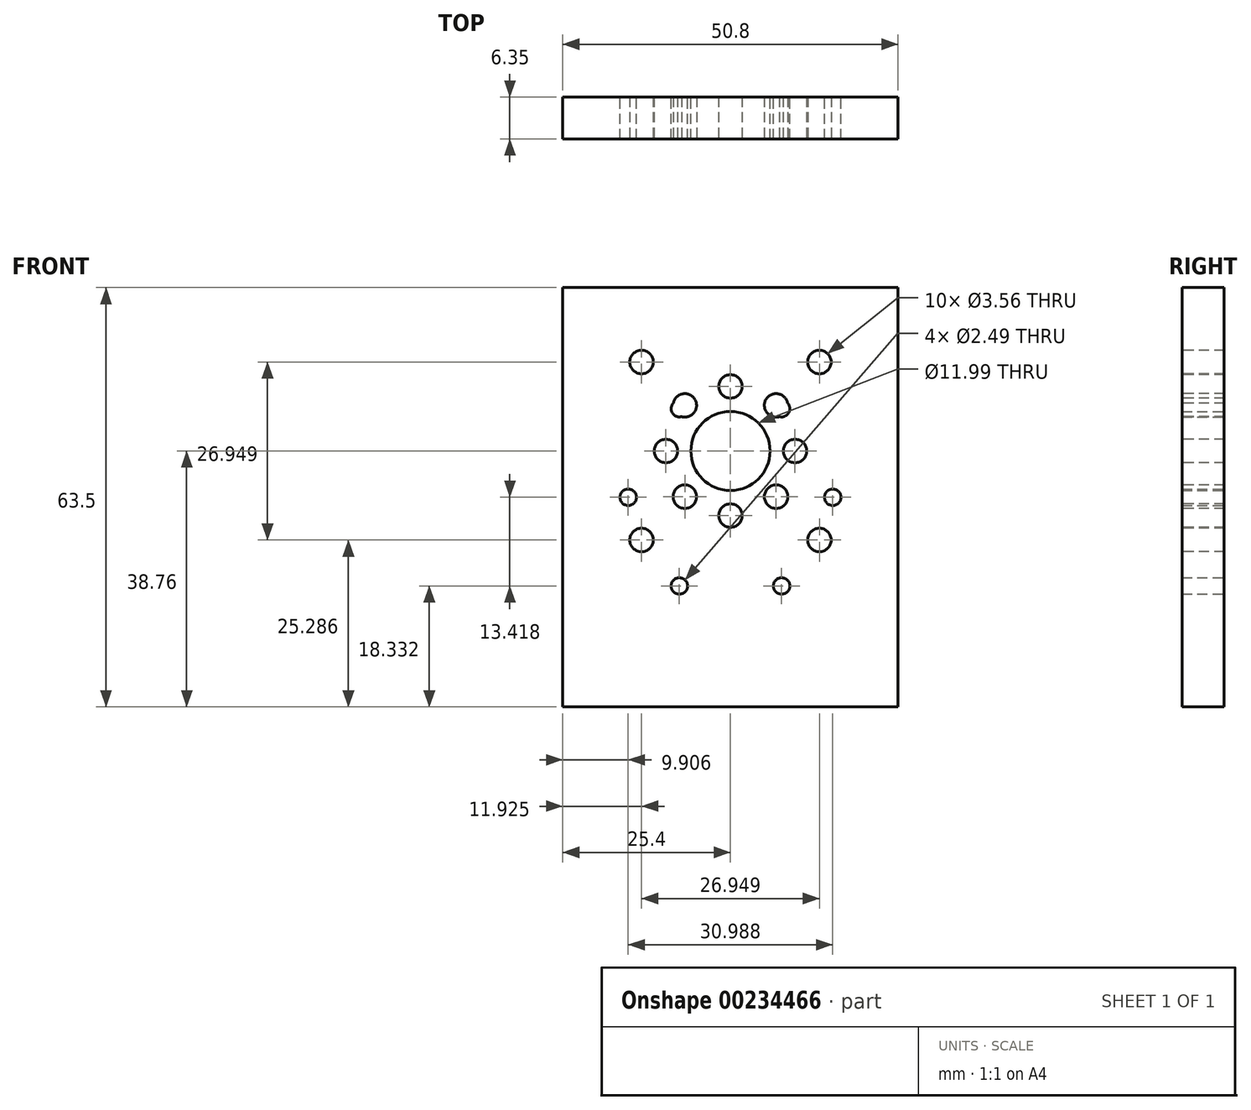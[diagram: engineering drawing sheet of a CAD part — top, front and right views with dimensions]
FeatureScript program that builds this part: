
annotation { "Feature Type Name" : "Feature", "Feature Type Description" : "" }
export const myFeature = defineFeature(function(context is Context, id is Id, definition is map)
    precondition{}
    {
        {
            var Q0;
            Q0=qCreatedBy(makeId("Front.planeOp"),FACE);
            var sketch = newSketch(context, id + "F0", { "sketchPlane" : qUnion([Q0])});
            skLineSegment(sketch, "E0.bottom", {"start": v(25.4, -31.75) * mm, "end": v(-25.4, -31.75) * mm});
            skLineSegment(sketch, "E0.top", {"start": v(25.4, 31.75) * mm, "end": v(-25.4, 31.75) * mm});
            skLineSegment(sketch, "E0.left", {"start": v(25.4, -31.75) * mm, "end": v(25.4, 31.75) * mm});
            skLineSegment(sketch, "E0.right", {"start": v(-25.4, -31.75) * mm, "end": v(-25.4, 31.75) * mm});
            skPoint(sketch, "E0.middle", {"position": v(0, 0) * mm});
            skCircle(sketch, "E1", {"center": v(0, 0) * mm, "radius": 15.5 * mm, "construction": true});
            skCircle(sketch, "E2", {"center": v(-15.5, 0) * mm, "radius": 1.24 * mm});
            skCircle(sketch, "E3.1.0", {"center": v(-7.75, -13.42) * mm, "radius": 1.24 * mm});
            skCircle(sketch, "E3.2.0", {"center": v(7.75, -13.42) * mm, "radius": 1.24 * mm});
            skCircle(sketch, "E3.3.0", {"center": v(15.5, 0) * mm, "radius": 1.24 * mm});
            skCircle(sketch, "E3.4.0", {"center": v(7.75, 13.42) * mm, "radius": 1.24 * mm});
            skCircle(sketch, "E3.5.0", {"center": v(-7.75, 13.42) * mm, "radius": 1.24 * mm});
            skSolve(sketch);
        }
        {
            var Q0;
            Q0=makeQuery(id+"F0.imprint","IMPRINT",FACE,{"disambiguationData":[TD([[makeQuery(id+"F0.imprint","IMPRINT",EDGE,{"derivedFrom":sQuery(id+"F0.wireOp",EDGE,"E0.bottom")}),-1.0]])]});
            var sketch = newSketch(context, id + "F1", { "sketchPlane" : qUnion([Q0])});
            skCircle(sketch, "E4", {"center": v(0, 7.01) * mm, "radius": 6 * mm});
            skSolve(sketch);
        }
        {
            var Q0;
            Q0=makeQuery(id+"F1.imprint","IMPRINT",FACE,{"disambiguationData":[TD([[makeQuery(id+"F1.imprint","IMPRINT",EDGE,{"derivedFrom":sQuery(id+"F1.wireOp",EDGE,"E4")}),-1.0]])]});
            extrude(context, id + "F2", {"entities" : qUnion([Q0]), "depth" : 6.35 * mm});
        }
        {
            var Q0;
            Q0=makeQuery(id+"F2.opExtrude","CAP_FACE",FACE,{"disambiguationData":[OSD([sQuery(id+"F0.wireOp",EDGE,"E0.bottom"),sQuery(id+"F0.wireOp",EDGE,"E0.top"),sQuery(id+"F0.wireOp",EDGE,"E0.left"),sQuery(id+"F0.wireOp",EDGE,"E0.right"),sQuery(id+"F0.wireOp",EDGE,"E2"),sQuery(id+"F0.wireOp",EDGE,"E3.1.0"),sQuery(id+"F0.wireOp",EDGE,"E3.2.0"),sQuery(id+"F0.wireOp",EDGE,"E3.3.0"),sQuery(id+"F0.wireOp",EDGE,"E3.4.0"),sQuery(id+"F0.wireOp",EDGE,"E3.5.0"),sQuery(id+"F1.wireOp",EDGE,"E4")])],"isStart":false});
            var sketch = newSketch(context, id + "F3", { "sketchPlane" : qUnion([Q0])});
            skCircle(sketch, "E5", {"center": v(0, 7.01) * mm, "radius": 9.78 * mm, "construction": true});
            skCircle(sketch, "E6", {"center": v(-9.78, 7.01) * mm, "radius": 1.78 * mm});
            skCircle(sketch, "E7.1.0", {"center": v(-6.91, 0.1) * mm, "radius": 1.78 * mm});
            skCircle(sketch, "E7.2.0", {"center": v(0, -2.77) * mm, "radius": 1.78 * mm});
            skCircle(sketch, "E7.3.0", {"center": v(6.91, 0.1) * mm, "radius": 1.78 * mm});
            skCircle(sketch, "E7.4.0", {"center": v(9.78, 7.01) * mm, "radius": 1.78 * mm});
            skCircle(sketch, "E7.5.0", {"center": v(6.91, 13.93) * mm, "radius": 1.78 * mm});
            skCircle(sketch, "E8.1.6.0", {"center": v(0, 16.79) * mm, "radius": 1.78 * mm});
            skCircle(sketch, "E8.1.7.0", {"center": v(-6.91, 13.93) * mm, "radius": 1.78 * mm});
            skLineSegment(sketch, "E9.bottom", {"start": v(13.47, -6.46) * mm, "end": v(-13.47, -6.46) * mm, "construction": true});
            skLineSegment(sketch, "E9.top", {"start": v(13.47, 20.49) * mm, "end": v(-13.47, 20.49) * mm, "construction": true});
            skLineSegment(sketch, "E9.left", {"start": v(13.47, -6.46) * mm, "end": v(13.47, 20.49) * mm, "construction": true});
            skLineSegment(sketch, "E9.right", {"start": v(-13.47, -6.46) * mm, "end": v(-13.47, 20.49) * mm, "construction": true});
            skCircle(sketch, "E10", {"center": v(-13.47, 20.49) * mm, "radius": 1.78 * mm});
            skCircle(sketch, "E11", {"center": v(13.47, 20.49) * mm, "radius": 1.78 * mm});
            skCircle(sketch, "E12", {"center": v(13.47, -6.46) * mm, "radius": 1.78 * mm});
            skCircle(sketch, "E13", {"center": v(-13.47, -6.46) * mm, "radius": 1.78 * mm});
            skSolve(sketch);
        }
        {
            var Q0;
            Q0 = qSketchRegion(id + "F3", true);
            extrude(context, id + "F4", {"entities" : qUnion([Q0]), "operationType" : NewBodyOperationType.REMOVE, "oppositeDirection" : true, "depth" : 25.4 * mm});
        }
    });
